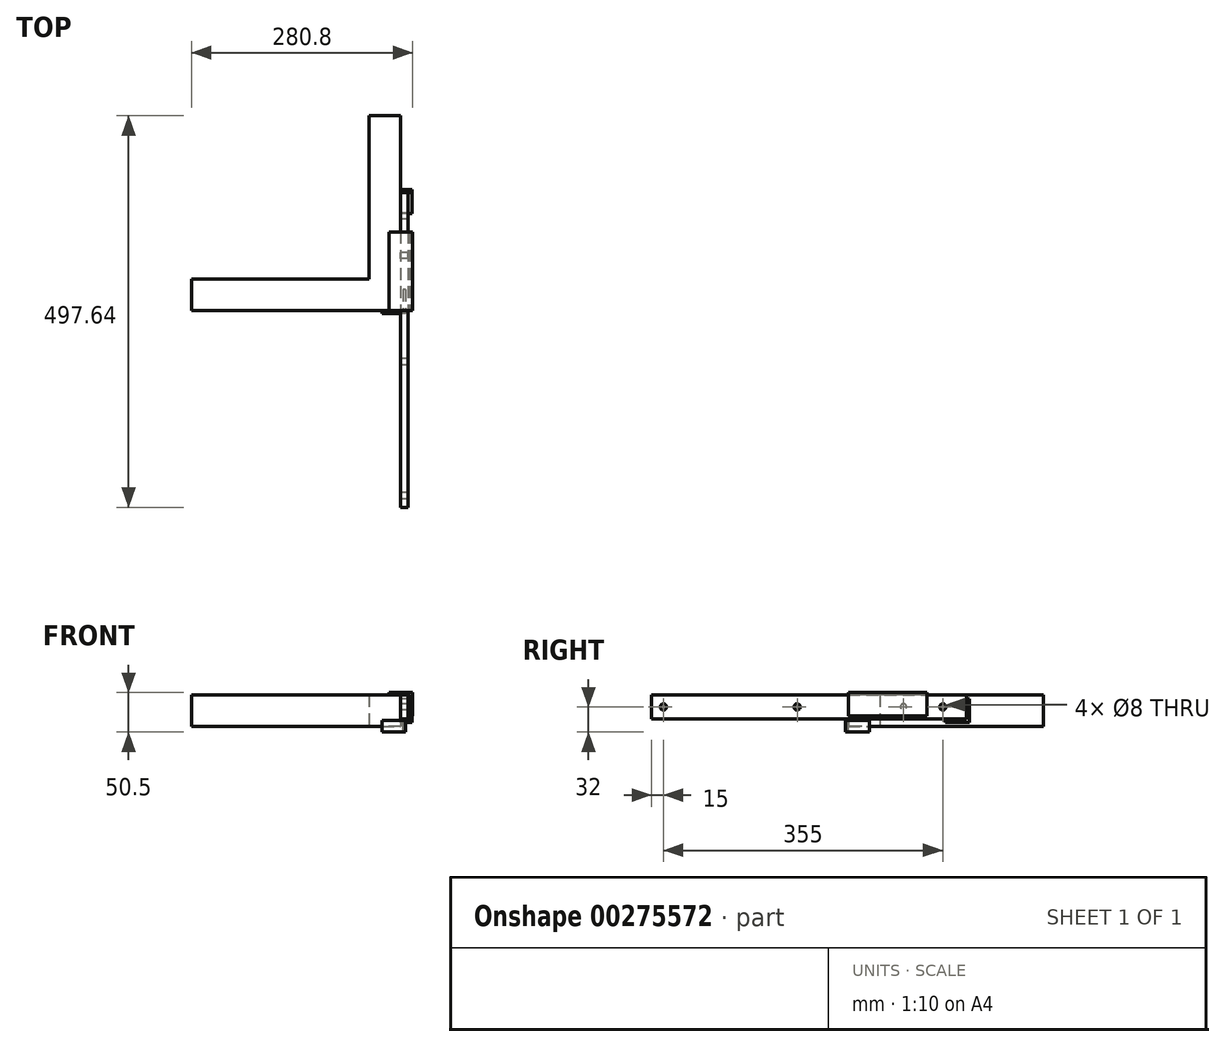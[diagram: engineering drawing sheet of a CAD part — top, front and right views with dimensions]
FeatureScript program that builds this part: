
annotation { "Feature Type Name" : "Feature", "Feature Type Description" : "" }
export const myFeature = defineFeature(function(context is Context, id is Id, definition is map)
    precondition{}
    {
        {
            var Q0;
            Q0=qCreatedBy(makeId("Top.planeOp"),FACE);
            var sketch = newSketch(context, id + "F0", { "sketchPlane" : qUnion([Q0])});
            skLineSegment(sketch, "E0.bottom", {"start": v(0, 0) * mm, "end": v(1240, 0) * mm});
            skLineSegment(sketch, "E0.top", {"start": v(0, 1100) * mm, "end": v(1240, 1100) * mm});
            skLineSegment(sketch, "E0.left", {"start": v(0, 0) * mm, "end": v(0, 1100) * mm});
            skLineSegment(sketch, "E0.right", {"start": v(1240, 0) * mm, "end": v(1240, 1100) * mm});
            skLineSegment(sketch, "E1.bottom", {"start": v(40, 1060) * mm, "end": v(1200, 1060) * mm});
            skLineSegment(sketch, "E1.top", {"start": v(40, 40) * mm, "end": v(1200, 40) * mm});
            skLineSegment(sketch, "E1.left", {"start": v(40, 1060) * mm, "end": v(40, 40) * mm});
            skLineSegment(sketch, "E1.right", {"start": v(1200, 1060) * mm, "end": v(1200, 40) * mm});
            skLineSegment(sketch, "E2", {"start": v(1240, 247.64) * mm, "end": v(1200, 247.64) * mm});
            skLineSegment(sketch, "E3", {"start": v(974.62, 40) * mm, "end": v(974.62, 0) * mm});
            skSolve(sketch);
        }
        {
            var Q0;
            Q0=makeQuery(id+"F0.imprint","IMPRINT",FACE,{"disambiguationData":[TD([[makeQuery(id+"F0.imprint","IMPRINT",EDGE,{"derivedFrom":sQuery(id+"F0.wireOp",EDGE,"E0.bottom")}),1.0]])]});
            extrude(context, id + "F1", {"entities" : qUnion([Q0]), "depth" : 40 * mm});
        }
        {
            var Q0;
            Q0=makeQuery(id+"F1.opExtrude","SWEPT_FACE",FACE,{"disambiguationData":[OSD([sQuery(id+"F0.wireOp",EDGE,"E0.right")])]});
            var sketch = newSketch(context, id + "F2", { "sketchPlane" : qUnion([Q0])});
            skLineSegment(sketch, "E4.bottom", {"start": v(150, 10) * mm, "end": v(-250, 10) * mm});
            skLineSegment(sketch, "E4.top", {"start": v(150, 40) * mm, "end": v(-250, 40) * mm});
            skLineSegment(sketch, "E4.left", {"start": v(150, 10) * mm, "end": v(150, 40) * mm});
            skLineSegment(sketch, "E4.right", {"start": v(-250, 10) * mm, "end": v(-250, 40) * mm});
            skLineSegment(sketch, "E5", {"start": v(150, 25) * mm, "end": v(-250, 25) * mm, "construction": true});
            skLineSegment(sketch, "E6.0", {"start": v(40, 40) * mm, "end": v(40, 0) * mm, "construction": true});
            skCircle(sketch, "E7", {"center": v(120, 25) * mm, "radius": 4 * mm});
            skCircle(sketch, "E8", {"center": v(70, 25) * mm, "radius": 4 * mm});
            skLineSegment(sketch, "E9", {"start": v(40, 9.53) * mm, "end": v(150, 9.53) * mm, "construction": true});
            skLineSegment(sketch, "E10", {"start": v(95, 9.53) * mm, "end": v(95, 40) * mm, "construction": true});
            skCircle(sketch, "E11", {"center": v(-235, 25) * mm, "radius": 4 * mm});
            skCircle(sketch, "E12", {"center": v(-65, 25) * mm, "radius": 4 * mm});
            skSolve(sketch);
        }
        {
            var Q0;
            {var subQ0=sQuery(id+"F2.wireOp",EDGE,"E4.right");Q0=makeQuery(id+"F2.imprint","IMPRINT",FACE,{"disambiguationData":[TD([[makeQuery(id+"F2.imprint","IMPRINT",EDGE,{"derivedFrom":subQ0}),-1.0]])]});}
            var Q1;
            {var subQ0=sQuery(id+"F2.wireOp",EDGE,"E4.left");Q1=makeQuery(id+"F2.imprint","IMPRINT",FACE,{"disambiguationData":[TD([[makeQuery(id+"F2.imprint","IMPRINT",EDGE,{"derivedFrom":subQ0}),1.0]])]});}
            extrude(context, id + "F3", {"entities" : qUnion([Q0, Q1]), "depth" : 10 * mm});
        }
        {
            var Q0;
            Q0=makeQuery(id+"F1.opExtrude","SWEPT_FACE",FACE,{"disambiguationData":[OSD([sQuery(id+"F0.wireOp",EDGE,"E0.bottom")])]});
            var sketch = newSketch(context, id + "F4", { "sketchPlane" : qUnion([Q0])});
            skLineSegment(sketch, "E13.0", {"start": v(1250, 10) * mm, "end": v(1250, 40) * mm, "construction": true});
            skLineSegment(sketch, "E14", {"start": v(1252, 40) * mm, "end": v(1225.42, 40) * mm});
            skLineSegment(sketch, "E15", {"start": v(1225.42, 40) * mm, "end": v(1225.42, 43.5) * mm});
            skLineSegment(sketch, "E16", {"start": v(1225.42, 43.5) * mm, "end": v(1255.42, 43.5) * mm});
            skLineSegment(sketch, "E17", {"start": v(1255.42, 43.5) * mm, "end": v(1255.42, 13.5) * mm});
            skLineSegment(sketch, "E18", {"start": v(1255.42, 13.5) * mm, "end": v(1251.92, 13.5) * mm});
            skLineSegment(sketch, "E19", {"start": v(1251.92, 13.5) * mm, "end": v(1252, 40) * mm});
            skSolve(sketch);
        }
        {
            var Q0;
            {var subQ4=sQuery(id+"F4.wireOp",EDGE,"E15");Q0=makeQuery(id+"F4.imprint","IMPRINT",FACE,{"disambiguationData":[TD([[makeQuery(id+"F4.imprint","IMPRINT",EDGE,{"derivedFrom":subQ4}),-1.0]])]});}
            extrude(context, id + "F5", {"entities" : qUnion([Q0]), "oppositeDirection" : true, "depth" : 100 * mm});
        }
        {
            var Q0;
            Q0=makeQuery(id+"F1.opExtrude","SWEPT_FACE",FACE,{"disambiguationData":[OSD([sQuery(id+"F0.wireOp",EDGE,"E0.right")])]});
            var sketch = newSketch(context, id + "F6", { "sketchPlane" : qUnion([Q0])});
            skLineSegment(sketch, "E20.0", {"start": v(150, 10) * mm, "end": v(150, 40) * mm});
            skLineSegment(sketch, "E21.0", {"start": v(150, 10) * mm, "end": v(-250, 10) * mm, "construction": true});
            skLineSegment(sketch, "E22", {"start": v(150, 10) * mm, "end": v(150, 9) * mm});
            skLineSegment(sketch, "E23", {"start": v(153.5, 5.5) * mm, "end": v(123.5, 5.5) * mm});
            skLineSegment(sketch, "E24", {"start": v(123.5, 5.5) * mm, "end": v(123.5, 9) * mm});
            skLineSegment(sketch, "E25", {"start": v(153.5, 5.5) * mm, "end": v(153.5, 35.5) * mm});
            skLineSegment(sketch, "E26", {"start": v(153.5, 35.5) * mm, "end": v(150, 35.5) * mm});
            skLineSegment(sketch, "E27", {"start": v(123.5, 9) * mm, "end": v(150, 9) * mm});
            skSolve(sketch);
        }
        {
            var Q0;
            {var subQ0=sQuery(id+"F6.wireOp",EDGE,"E22");Q0=makeQuery(id+"F6.imprint","IMPRINT",FACE,{"disambiguationData":[TD([[makeQuery(id+"F6.imprint","IMPRINT",EDGE,{"derivedFrom":subQ0}),1.0]])]});}
            extrude(context, id + "F7", {"entities" : qUnion([Q0]), "depth" : 15 * mm});
        }
        {
            var Q0;
            Q0=makeQuery(id+"F3.opExtrude","SWEPT_FACE",FACE,{"disambiguationData":[OSD([sQuery(id+"F2.wireOp",EDGE,"E4.bottom")])]});
            cPlane(context, id + "F8", {"entities" : qUnion([Q0]), "cplaneType" : CPlaneType.OFFSET, "offset" : 2 * mm, "width" : 150 * mm, "height" : 150 * mm});
        }
        {
            var Q0;
            Q0=qCreatedBy(id+"F8.planeOp",FACE);
            var sketch = newSketch(context, id + "F9", { "sketchPlane" : qUnion([Q0])});
            skLineSegment(sketch, "E28.0", {"start": v(1240, 0) * mm, "end": v(1240, -247.64) * mm, "construction": true});
            skLineSegment(sketch, "E29.0", {"start": v(974.62, 0) * mm, "end": v(1240, 0) * mm, "construction": true});
            skLineSegment(sketch, "E30", {"start": v(1246.75, -26.5) * mm, "end": v(1246.75, 3.5) * mm});
            skLineSegment(sketch, "E31", {"start": v(1246.75, 3.5) * mm, "end": v(1216.75, 3.5) * mm});
            skLineSegment(sketch, "E32", {"start": v(1246.75, -26.5) * mm, "end": v(1243.25, -26.5) * mm});
            skLineSegment(sketch, "E33", {"start": v(1243.25, -26.5) * mm, "end": v(1243.25, 0) * mm});
            skLineSegment(sketch, "E34", {"start": v(1243.25, 0) * mm, "end": v(1216.75, 0) * mm});
            skLineSegment(sketch, "E35", {"start": v(1216.75, 0) * mm, "end": v(1216.75, 3.5) * mm});
            skLineSegment(sketch, "E36.0", {"start": v(1250, -150) * mm, "end": v(1250, 250) * mm, "construction": true});
            skLineSegment(sketch, "E37", {"start": v(1250, -33.86) * mm, "end": v(1240, -33.86) * mm, "construction": true});
            skLineSegment(sketch, "E38", {"start": v(1245, -26.5) * mm, "end": v(1245, 3.5) * mm, "construction": true});
            skLineSegment(sketch, "E39", {"start": v(1245, -33.86) * mm, "end": v(1245, -50.56) * mm, "construction": true});
            skSolve(sketch);
        }
        {
            var Q0;
            Q0=makeQuery(id+"F9.imprint","IMPRINT",FACE,{"disambiguationData":[TD([[makeQuery(id+"F9.imprint","IMPRINT",EDGE,{"derivedFrom":sQuery(id+"F9.wireOp",EDGE,"E30")}),1.0]])]});
            extrude(context, id + "F10", {"entities" : qUnion([Q0]), "depth" : 15 * mm});
        }
    });
